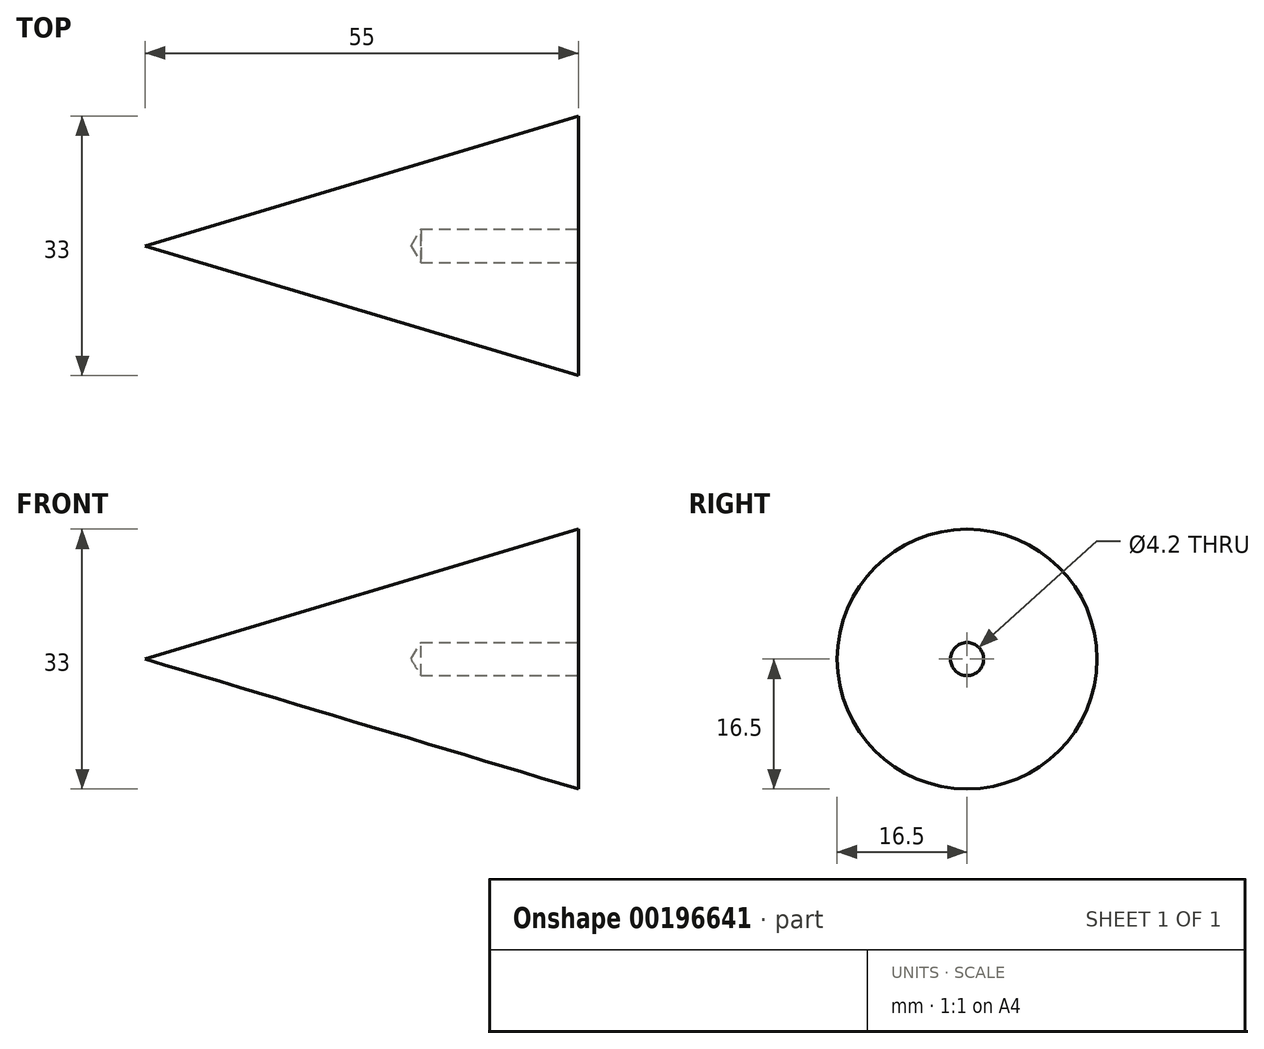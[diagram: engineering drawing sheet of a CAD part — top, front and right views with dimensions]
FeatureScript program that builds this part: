
annotation { "Feature Type Name" : "Feature", "Feature Type Description" : "" }
export const myFeature = defineFeature(function(context is Context, id is Id, definition is map)
    precondition{}
    {
        {
            var Q0;
            Q0=qCreatedBy(makeId("Front.planeOp"),FACE);
            var sketch = newSketch(context, id + "F0", { "sketchPlane" : qUnion([Q0])});
            skLineSegment(sketch, "E0", {"start": v(0, 0) * mm, "end": v(55, 16.5) * mm});
            skLineSegment(sketch, "E1", {"start": v(55, 16.5) * mm, "end": v(55, 0) * mm});
            skLineSegment(sketch, "E2", {"start": v(55, 0) * mm, "end": v(0, 0) * mm});
            skSolve(sketch);
        }
        {
            var Q0;
            Q0=makeQuery(id+"F0.imprint","IMPRINT",FACE,{"disambiguationData":[TD([[makeQuery(id+"F0.imprint","IMPRINT",EDGE,{"derivedFrom":sQuery(id+"F0.wireOp",EDGE,"E0")}),-1.0]])]});
            var Q1;
            Q1=sQuery(id+"F0.wireOp",EDGE,"E2");
            revolve(context, id + "F1", {"entities" : qUnion([Q0]), "axis" : qUnion([Q1]), "revolveType" : RevolveType.FULL});
        }
        {
            var Q0;
            Q0=makeQuery(id+"F1.opRevolve","SWEPT_FACE",FACE,{"disambiguationData":[OSD([sQuery(id+"F0.wireOp",EDGE,"E1")])]});
            var sketch = newSketch(context, id + "F2", { "sketchPlane" : qUnion([Q0])});
            skPoint(sketch, "E3", {"position": v(0, 0) * mm});
            skSolve(sketch);
        }
        {
            var Q0;
            Q0=sQuery(id+"F2.wireOp",VERTEX,"E3");
            var Q1;
            Q1=makeQuery(id+"F1.opRevolve","SWEPT_BODY",BODY,{"disambiguationData":[OSD([sQuery(id+"F0.wireOp",EDGE,"E0"),sQuery(id+"F0.wireOp",EDGE,"E1"),sQuery(id+"F0.wireOp",EDGE,"E2")])]});
            hole(context, id + "F3", {"style" : HoleStyle.SIMPLE, "endStyle" : HoleEndStyle.BLIND, "standardTappedOrClearance" : lookupTablePath({ "standard" : "ISO", "engagement" : "75%", "pitch" : "0.8 mm", "size" : "M5", "type" : "Tapped" }), "standardBlindInLast" : lookupTablePath({ "standard" : "ISO", "engagement" : "75%", "pitch" : "0.8 mm", "size" : "M5", "type" : "Tapped" }), "holeDiameter" : 4.2 * mm, "holeDepth" : 20 * mm, "startFromSketch" : true, "locations" : qUnion([Q0]), "scope" : qUnion([Q1]), "majorDiameter" : 5 * mm});
        }
    });
